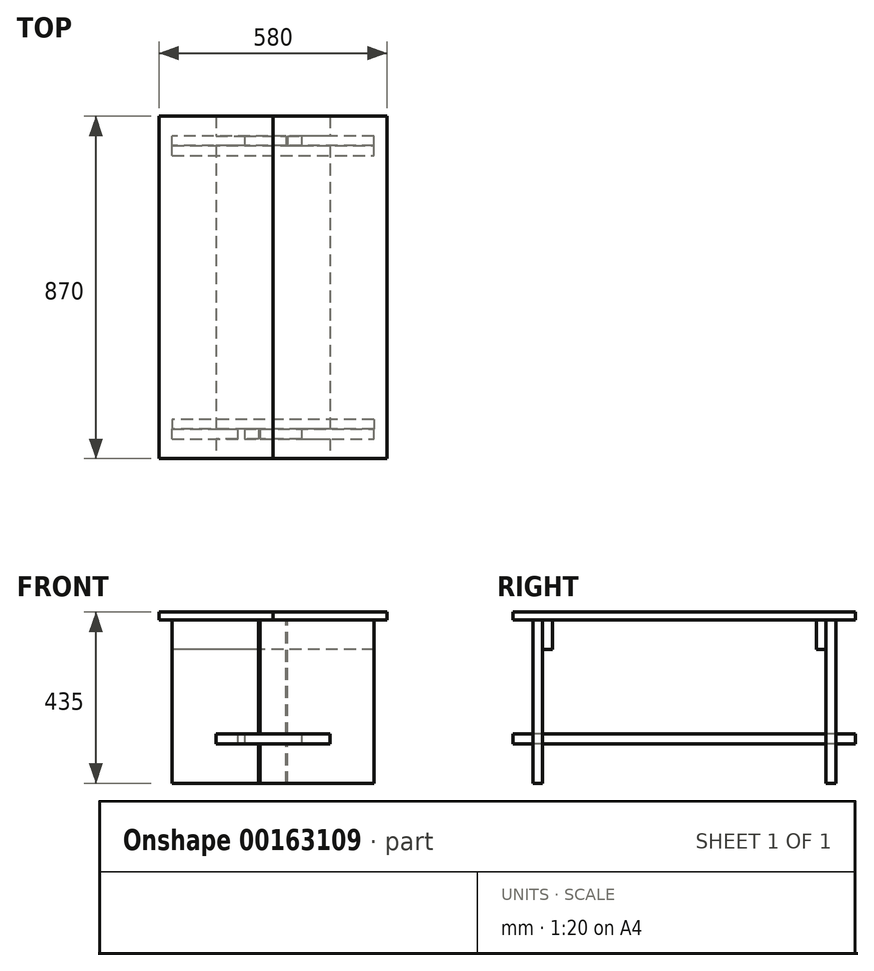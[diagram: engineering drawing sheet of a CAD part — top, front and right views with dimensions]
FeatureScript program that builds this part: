
annotation { "Feature Type Name" : "Feature", "Feature Type Description" : "" }
export const myFeature = defineFeature(function(context is Context, id is Id, definition is map)
    precondition{}
    {
        {
            var Q0;
            Q0=qCreatedBy(makeId("Front.planeOp"),FACE);
            var sketch = newSketch(context, id + "F0", { "sketchPlane" : qUnion([Q0])});
            skLineSegment(sketch, "E0.bottom", {"start": v(0, 0) * mm, "end": v(-290, 0) * mm});
            skLineSegment(sketch, "E0.top", {"start": v(0, -20) * mm, "end": v(-290, -20) * mm});
            skLineSegment(sketch, "E0.left", {"start": v(0, 0) * mm, "end": v(0, -20) * mm});
            skLineSegment(sketch, "E0.right", {"start": v(-290, 0) * mm, "end": v(-290, -20) * mm});
            skSolve(sketch);
        }
        {
            var Q0;
            Q0 = qSketchRegion(id + "F0", true);
            extrude(context, id + "F1", {"entities" : qUnion([Q0]), "endBound" : BoundingType.SYMMETRIC, "depth" : 870 * mm});
        }
        {
            var Q0;
            Q0=qCreatedBy(makeId("Front.planeOp"),FACE);
            var sketch = newSketch(context, id + "F2", { "sketchPlane" : qUnion([Q0])});
            skLineSegment(sketch, "E1.bottom", {"start": v(0, 0) * mm, "end": v(290, 0) * mm});
            skLineSegment(sketch, "E1.top", {"start": v(0, -20) * mm, "end": v(290, -20) * mm});
            skLineSegment(sketch, "E1.left", {"start": v(0, 0) * mm, "end": v(0, -20) * mm});
            skLineSegment(sketch, "E1.right", {"start": v(290, 0) * mm, "end": v(290, -20) * mm});
            skSolve(sketch);
        }
        {
            var Q0;
            Q0 = qSketchRegion(id + "F2", true);
            extrude(context, id + "F3", {"entities" : qUnion([Q0]), "endBound" : BoundingType.SYMMETRIC, "depth" : 870 * mm});
        }
        {
            var Q0;
            Q0=makeQuery(id+"F3.opExtrude","SWEPT_FACE",FACE,{"disambiguationData":[OSD([sQuery(id+"F2.wireOp",EDGE,"E1.top")])]});
            var sketch = newSketch(context, id + "F4", { "sketchPlane" : qUnion([Q0])});
            skLineSegment(sketch, "E2.bottom", {"start": v(-256.5, 385) * mm, "end": v(-36.5, 385) * mm});
            skLineSegment(sketch, "E2.top", {"start": v(-256.5, 360) * mm, "end": v(-36.5, 360) * mm});
            skLineSegment(sketch, "E2.left", {"start": v(-256.5, 385) * mm, "end": v(-256.5, 360) * mm});
            skLineSegment(sketch, "E2.right", {"start": v(-36.5, 385) * mm, "end": v(-36.5, 360) * mm});
            skLineSegment(sketch, "E3.bottom", {"start": v(-33.5, 385) * mm, "end": v(256.5, 385) * mm});
            skLineSegment(sketch, "E3.top", {"start": v(-33.5, 360) * mm, "end": v(256.5, 360) * mm});
            skLineSegment(sketch, "E3.left", {"start": v(-33.5, 385) * mm, "end": v(-33.5, 360) * mm});
            skLineSegment(sketch, "E3.right", {"start": v(256.5, 385) * mm, "end": v(256.5, 360) * mm});
            skLineSegment(sketch, "E4.bottom", {"start": v(256.5, -360) * mm, "end": v(36.5, -360) * mm});
            skLineSegment(sketch, "E4.top", {"start": v(256.5, -385) * mm, "end": v(36.5, -385) * mm});
            skLineSegment(sketch, "E4.left", {"start": v(256.5, -360) * mm, "end": v(256.5, -385) * mm});
            skLineSegment(sketch, "E4.right", {"start": v(36.5, -360) * mm, "end": v(36.5, -385) * mm});
            skLineSegment(sketch, "E5.bottom", {"start": v(33.5, -360) * mm, "end": v(-256.5, -360) * mm});
            skLineSegment(sketch, "E5.top", {"start": v(33.5, -385) * mm, "end": v(-256.5, -385) * mm});
            skLineSegment(sketch, "E5.left", {"start": v(33.5, -360) * mm, "end": v(33.5, -385) * mm});
            skLineSegment(sketch, "E5.right", {"start": v(-256.5, -360) * mm, "end": v(-256.5, -385) * mm});
            skLineSegment(sketch, "E6", {"start": v(256.5, -360) * mm, "end": v(256.5, -198.26) * mm, "construction": true});
            skLineSegment(sketch, "E7", {"start": v(256.5, -198.26) * mm, "end": v(0, -198.26) * mm, "construction": true});
            skLineSegment(sketch, "E8", {"start": v(0, -198.26) * mm, "end": v(-256.5, -198.26) * mm, "construction": true});
            skLineSegment(sketch, "E9", {"start": v(-256.5, -198.26) * mm, "end": v(-256.5, -360) * mm, "construction": true});
            skSolve(sketch);
        }
        {
            var Q0;
            Q0 = qSketchRegion(id + "F4", true);
            extrude(context, id + "F5", {"entities" : qUnion([Q0]), "depth" : 415 * mm});
        }
        {
            var Q0;
            Q0=qCreatedBy(makeId("Front.planeOp"),FACE);
            var sketch = newSketch(context, id + "F6", { "sketchPlane" : qUnion([Q0])});
            skLineSegment(sketch, "E10.bottom", {"start": v(72.5, -310) * mm, "end": v(-72.5, -310) * mm});
            skLineSegment(sketch, "E10.top", {"start": v(72.5, -335) * mm, "end": v(-72.5, -335) * mm});
            skLineSegment(sketch, "E10.left", {"start": v(72.5, -310) * mm, "end": v(72.5, -335) * mm});
            skLineSegment(sketch, "E10.right", {"start": v(-72.5, -310) * mm, "end": v(-72.5, -335) * mm});
            skSolve(sketch);
        }
        {
            var Q0;
            Q0=makeQuery(id+"F6.imprint","IMPRINT",FACE,{"disambiguationData":[TD([[makeQuery(id+"F6.imprint","IMPRINT",EDGE,{"derivedFrom":sQuery(id+"F6.wireOp",EDGE,"E10.bottom")}),1.0]])]});
            extrude(context, id + "F7", {"entities" : qUnion([Q0]), "operationType" : NewBodyOperationType.REMOVE, "endBound" : BoundingType.SYMMETRIC, "oppositeDirection" : true, "depth" : 1000 * mm});
        }
        {
            var Q0;
            Q0=makeQuery(id+"F7.boolean.opBoolean","COPY",FACE,{"disambiguationData":[TD([makeQuery(id+"F5.opExtrude","SWEPT_FACE",FACE,{"disambiguationData":[OSD([sQuery(id+"F4.wireOp",EDGE,"E5.bottom")])]})])],"derivedFrom":makeQuery(id+"F7.opExtrude","SWEPT_FACE",FACE,{"disambiguationData":[OSD([sQuery(id+"F6.wireOp",EDGE,"E10.top")])]})});
            var sketch = newSketch(context, id + "F8", { "sketchPlane" : qUnion([Q0])});
            skLineSegment(sketch, "E11.bottom", {"start": v(-145, 435) * mm, "end": v(145, 435) * mm});
            skLineSegment(sketch, "E11.top", {"start": v(-145, -435) * mm, "end": v(145, -435) * mm});
            skLineSegment(sketch, "E11.left", {"start": v(-145, 435) * mm, "end": v(-145, 385) * mm});
            skLineSegment(sketch, "E11.right", {"start": v(145, 435) * mm, "end": v(145, 385) * mm});
            skLineSegment(sketch, "E12", {"start": v(-145, 385) * mm, "end": v(-72.5, 385) * mm});
            skPoint(sketch, "E12.endSnap0", {"position": v(-72.5, 372.5) * mm});
            skLineSegment(sketch, "E13", {"start": v(-72.5, 385) * mm, "end": v(-72.5, 360) * mm});
            skLineSegment(sketch, "E14", {"start": v(-72.5, 360) * mm, "end": v(-145, 360) * mm});
            skLineSegment(sketch, "E15", {"start": v(145, 385) * mm, "end": v(72.5, 385) * mm});
            skLineSegment(sketch, "E16", {"start": v(72.5, 385) * mm, "end": v(72.5, 360) * mm});
            skLineSegment(sketch, "E17", {"start": v(72.5, 360) * mm, "end": v(145, 360) * mm});
            skLineSegment(sketch, "E18", {"start": v(-145, -360) * mm, "end": v(-90.64, -360) * mm});
            skLineSegment(sketch, "E19", {"start": v(-90.64, -360) * mm, "end": v(-90.64, -385) * mm});
            skLineSegment(sketch, "E20", {"start": v(-90.64, -385) * mm, "end": v(-145, -385) * mm});
            skLineSegment(sketch, "E21", {"start": v(145, -360) * mm, "end": v(72.5, -360) * mm});
            skLineSegment(sketch, "E22", {"start": v(72.5, -360) * mm, "end": v(72.5, -385) * mm});
            skLineSegment(sketch, "E23", {"start": v(72.5, -385) * mm, "end": v(145, -385) * mm});
            skLineSegment(sketch, "E24.trimOffspring", {"start": v(145, 360) * mm, "end": v(145, -360) * mm});
            skLineSegment(sketch, "E25.trimOffspring", {"start": v(-145, 360) * mm, "end": v(-145, -360) * mm});
            skLineSegment(sketch, "E26.trimOffspring", {"start": v(-145, -385) * mm, "end": v(-145, -435) * mm});
            skLineSegment(sketch, "E27.trimOffspring", {"start": v(145, -385) * mm, "end": v(145, -435) * mm});
            skSolve(sketch);
        }
        {
            var Q0;
            Q0 = qSketchRegion(id + "F8", true);
            extrude(context, id + "F9", {"entities" : qUnion([Q0]), "depth" : 25 * mm});
        }
        {
            var Q0;
            Q0=makeQuery(id+"F5.opExtrude","SWEPT_FACE",FACE,{"disambiguationData":[OSD([sQuery(id+"F4.wireOp",EDGE,"E3.top")])]});
            var sketch = newSketch(context, id + "F10", { "sketchPlane" : qUnion([Q0])});
            skLineSegment(sketch, "E28.bottom", {"start": v(-256.5, -20) * mm, "end": v(256.5, -20) * mm});
            skLineSegment(sketch, "E28.top", {"start": v(-256.5, -95) * mm, "end": v(256.5, -95) * mm});
            skLineSegment(sketch, "E28.left", {"start": v(-256.5, -20) * mm, "end": v(-256.5, -95) * mm});
            skLineSegment(sketch, "E28.right", {"start": v(256.5, -20) * mm, "end": v(256.5, -95) * mm});
            skSolve(sketch);
        }
        {
            var Q0;
            Q0 = qSketchRegion(id + "F10", true);
            extrude(context, id + "F11", {"entities" : qUnion([Q0]), "depth" : 25 * mm});
        }
        {
            var Q0;
            Q0=makeQuery(id+"F5.opExtrude","SWEPT_FACE",FACE,{"disambiguationData":[OSD([sQuery(id+"F4.wireOp",EDGE,"E5.bottom")])]});
            var sketch = newSketch(context, id + "F12", { "sketchPlane" : qUnion([Q0])});
            skLineSegment(sketch, "E29.bottom", {"start": v(-256.5, -20) * mm, "end": v(256.5, -20) * mm});
            skLineSegment(sketch, "E29.top", {"start": v(-256.5, -95) * mm, "end": v(256.5, -95) * mm});
            skLineSegment(sketch, "E29.left", {"start": v(-256.5, -20) * mm, "end": v(-256.5, -95) * mm});
            skLineSegment(sketch, "E29.right", {"start": v(256.5, -20) * mm, "end": v(256.5, -95) * mm});
            skSolve(sketch);
        }
        {
            var Q0;
            Q0 = qSketchRegion(id + "F12", true);
            extrude(context, id + "F13", {"entities" : qUnion([Q0]), "depth" : 25 * mm});
        }
    });
